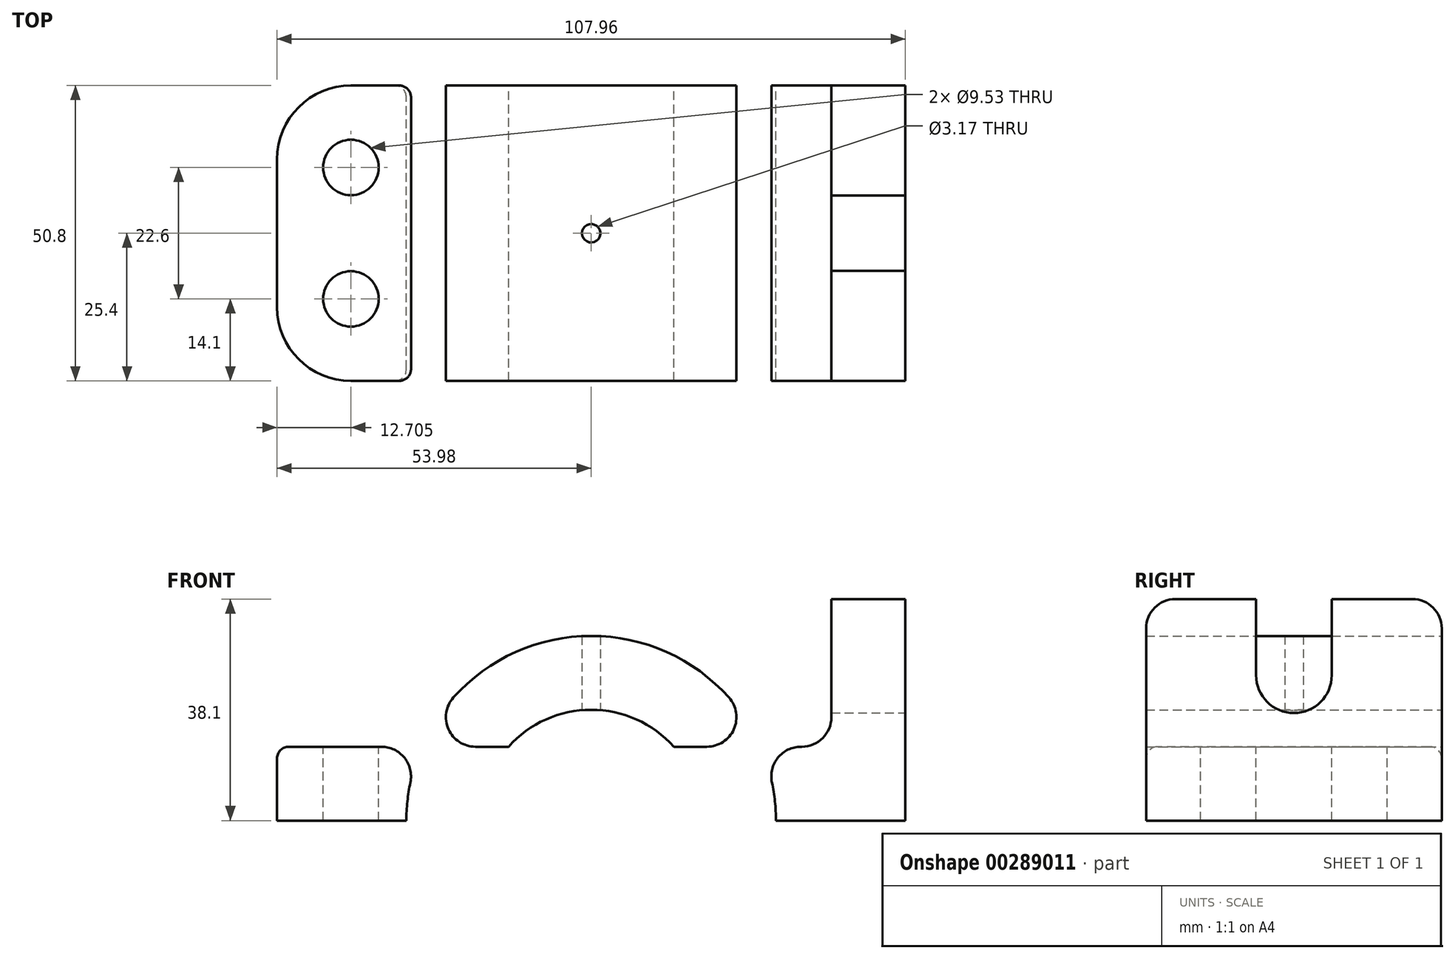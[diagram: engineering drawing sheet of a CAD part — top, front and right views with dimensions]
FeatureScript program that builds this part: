
annotation { "Feature Type Name" : "Feature", "Feature Type Description" : "" }
export const myFeature = defineFeature(function(context is Context, id is Id, definition is map)
    precondition{}
    {
        {
            var Q0;
            Q0=qCreatedBy(makeId("Front.planeOp"),FACE);
            var sketch = newSketch(context, id + "F0", { "sketchPlane" : qUnion([Q0])});
            skLineSegment(sketch, "E0", {"start": v(-53.97, 0) * mm, "end": v(53.97, 0) * mm});
            skLineSegment(sketch, "E1", {"start": v(53.98, 0) * mm, "end": v(53.98, 38.1) * mm});
            skLineSegment(sketch, "E2", {"start": v(53.97, 38.1) * mm, "end": v(41.28, 38.1) * mm});
            skLineSegment(sketch, "E3", {"start": v(41.28, 38.1) * mm, "end": v(41.28, 12.7) * mm});
            skLineSegment(sketch, "E4", {"start": v(41.28, 12.7) * mm, "end": v(-53.98, 12.7) * mm});
            skLineSegment(sketch, "E5", {"start": v(-53.98, 12.7) * mm, "end": v(-53.98, 0) * mm});
            skCircle(sketch, "E6", {"center": v(0, 0) * mm, "radius": 31.75 * mm});
            skCircle(sketch, "E7", {"center": v(0, 0) * mm, "radius": 19.05 * mm});
            skSolve(sketch);
        }
        {
            var Q0;
            {var subQ5=sQuery(id+"F0.wireOp",EDGE,"E5");Q0=makeQuery(id+"F0.imprint","IMPRINT",FACE,{"disambiguationData":[TD([[makeQuery(id+"F0.imprint","IMPRINT",EDGE,{"derivedFrom":subQ5}),1.0]])]});}
            var Q1;
            {var subQ6=sQuery(id+"F0.wireOp",EDGE,"E1");Q1=makeQuery(id+"F0.imprint","IMPRINT",FACE,{"disambiguationData":[TD([[makeQuery(id+"F0.imprint","IMPRINT",EDGE,{"derivedFrom":subQ6}),1.0]])]});}
            var Q2;
            {var subQ1=sQuery(id+"F0.wireOp",EDGE,"E4");var subQ4=sQuery(id+"F0.wireOp",EDGE,"E6");var subQ6=makeQuery(id+"F0.imprint","INTERSECT",VERTEX,{"disambiguationData":[OD(0.0)],"derivedFrom":[subQ1,subQ4]});Q2=makeQuery(id+"F0.imprint","IMPRINT",FACE,{"disambiguationData":[TD([[makeQuery(id+"F0.imprint","IMPRINT",EDGE,{"disambiguationData":[TD([[subQ6,-1.0]])],"derivedFrom":subQ1}),-1.0]])]});}
            var Q3;
            {var subQ3=sQuery(id+"F0.wireOp",EDGE,"E0");var subQ5=sQuery(id+"F0.wireOp",EDGE,"E6");var subQ7=makeQuery(id+"F0.imprint","INTERSECT",VERTEX,{"disambiguationData":[OD(1.0)],"derivedFrom":[subQ3,subQ5]});Q3=makeQuery(id+"F0.imprint","IMPRINT",FACE,{"disambiguationData":[TD([[makeQuery(id+"F0.imprint","IMPRINT",EDGE,{"disambiguationData":[TD([[subQ7,1.0]])],"derivedFrom":subQ3}),1.0]])]});}
            var Q4;
            {var subQ3=sQuery(id+"F0.wireOp",EDGE,"E0");var subQ5=sQuery(id+"F0.wireOp",EDGE,"E6");var subQ7=makeQuery(id+"F0.imprint","INTERSECT",VERTEX,{"disambiguationData":[OD(0.0)],"derivedFrom":[subQ3,subQ5]});Q4=makeQuery(id+"F0.imprint","IMPRINT",FACE,{"disambiguationData":[TD([[makeQuery(id+"F0.imprint","IMPRINT",EDGE,{"disambiguationData":[TD([[subQ7,-1.0]])],"derivedFrom":subQ3}),1.0]])]});}
            extrude(context, id + "F1", {"entities" : qUnion([Q0, Q1, Q2, Q3, Q4]), "endBound" : BoundingType.SYMMETRIC, "depth" : 50.8 * mm});
        }
        {
            var Q0;
            {var subQ0=sQuery(id+"F0.wireOp",EDGE,"E4");Q0=makeQuery(id+"F1.opExtrude","SWEPT_FACE",FACE,{"disambiguationData":[OSD([subQ0]),TDD([makeQuery(id+"F0.imprint","IMPRINT",EDGE,{"disambiguationData":[TD([[makeQuery(id+"F0.imprint","INTERSECT",VERTEX,{"derivedFrom":[subQ0,sQuery(id+"F0.wireOp",EDGE,"E5")]}),1.0]])],"derivedFrom":subQ0})])]});}
            var sketch = newSketch(context, id + "F2", { "sketchPlane" : qUnion([Q0])});
            skCircle(sketch, "E8", {"center": v(-41.27, 11.3) * mm, "radius": 4.76 * mm});
            skCircle(sketch, "E9", {"center": v(-41.27, -11.3) * mm, "radius": 4.76 * mm});
            skSolve(sketch);
        }
        {
            var Q0;
            {Q0=qUnion([makeQuery(id+"F2.imprint","IMPRINT",FACE,{"disambiguationData":[TD([[makeQuery(id+"F2.imprint","IMPRINT",EDGE,{"derivedFrom":sQuery(id+"F2.wireOp",EDGE,"E8")}),1.0]])]}),makeQuery(id+"F2.imprint","IMPRINT",FACE,{"disambiguationData":[TD([[makeQuery(id+"F2.imprint","IMPRINT",EDGE,{"derivedFrom":sQuery(id+"F2.wireOp",EDGE,"E9")}),1.0]])]})]);}
            extrude(context, id + "F3", {"entities" : qUnion([Q0]), "operationType" : NewBodyOperationType.REMOVE, "endBound" : BoundingType.THROUGH_ALL, "oppositeDirection" : true, "depth" : 25 * mm});
        }
        {
            var Q0;
            Q0=makeQuery(id+"F1.opExtrude","SWEPT_FACE",FACE,{"disambiguationData":[OSD([sQuery(id+"F0.wireOp",EDGE,"E1")])]});
            var sketch = newSketch(context, id + "F4", { "sketchPlane" : qUnion([Q0])});
            skLineSegment(sketch, "E10.bottom", {"start": v(-6.5, 38.1) * mm, "end": v(6.5, 38.1) * mm});
            skLineSegment(sketch, "E10.top", {"start": v(-6.5, 25) * mm, "end": v(6.5, 25) * mm});
            skLineSegment(sketch, "E10.left", {"start": v(-6.5, 38.1) * mm, "end": v(-6.5, 25) * mm});
            skLineSegment(sketch, "E10.right", {"start": v(6.5, 38.1) * mm, "end": v(6.5, 25) * mm});
            skPoint(sketch, "E11", {"position": v(0, 38.1) * mm});
            skCircle(sketch, "E12", {"center": v(0, 25) * mm, "radius": 6.5 * mm});
            skSolve(sketch);
        }
        {
            var Q0;
            {var subQ1=sQuery(id+"F4.wireOp",EDGE,"E10.top");var subQ7=makeQuery(id+"F4.imprint","IMPRINT",EDGE,{"derivedFrom":subQ1});Q0=qUnion([makeQuery(id+"F4.imprint","IMPRINT",FACE,{"disambiguationData":[TD([[makeQuery(id+"F4.imprint","IMPRINT",EDGE,{"derivedFrom":sQuery(id+"F4.wireOp",EDGE,"E10.bottom")}),-1.0]])]}),makeQuery(id+"F4.imprint","IMPRINT",FACE,{"disambiguationData":[TD([[subQ7,1.0]])]}),makeQuery(id+"F4.imprint","IMPRINT",FACE,{"disambiguationData":[TD([[subQ7,-1.0]])]})]);}
            extrude(context, id + "F5", {"entities" : qUnion([Q0]), "operationType" : NewBodyOperationType.REMOVE, "endBound" : BoundingType.UP_TO_NEXT, "oppositeDirection" : true, "depth" : 25 * mm});
        }
        {
            var Q0;
            {var subQ0=sQuery(id+"F0.wireOp",EDGE,"E0");var subQ1=makeQuery(id+"F0.imprint","INTERSECT",VERTEX,{"disambiguationData":[OD(1.0)],"derivedFrom":[subQ0,sQuery(id+"F0.wireOp",EDGE,"E6")]});Q0=makeQuery(id+"F1.opExtrude","SWEPT_FACE",FACE,{"disambiguationData":[OSD([subQ0]),TDD([makeQuery(id+"F0.imprint","IMPRINT",EDGE,{"disambiguationData":[TD([[subQ1,1.0]])],"derivedFrom":subQ0}),makeQuery(id+"F0.imprint","IMPRINT",EDGE,{"disambiguationData":[TD([[makeQuery(id+"F0.imprint","INTERSECT",VERTEX,{"derivedFrom":[subQ0,sQuery(id+"F0.wireOp",EDGE,"E1")]}),1.0]])],"derivedFrom":subQ0})])]});}
            var sketch = newSketch(context, id + "F6", { "sketchPlane" : qUnion([Q0])});
            skCircle(sketch, "E13", {"center": v(0, 0) * mm, "radius": 1.59 * mm});
            skSolve(sketch);
        }
        {
            var Q0;
            Q0=makeQuery(id+"F6.imprint","IMPRINT",FACE,{"disambiguationData":[TD([[makeQuery(id+"F6.imprint","IMPRINT",EDGE,{"derivedFrom":sQuery(id+"F6.wireOp",EDGE,"E13")}),1.0]])]});
            extrude(context, id + "F7", {"entities" : qUnion([Q0]), "operationType" : NewBodyOperationType.REMOVE, "endBound" : BoundingType.THROUGH_ALL, "oppositeDirection" : true, "depth" : 47.28 * mm});
        }
        {
            var Q0;
            Q0=makeQuery(id+"F1.opExtrude","CAP_EDGE",EDGE,{"disambiguationData":[OSD([sQuery(id+"F0.wireOp",EDGE,"E2")])],"isStart":false});
            var Q1;
            Q1=makeQuery(id+"F1.opExtrude","CAP_EDGE",EDGE,{"disambiguationData":[OSD([sQuery(id+"F0.wireOp",EDGE,"E2")])],"isStart":true});
            var Q2;
            {var subQ0=sQuery(id+"F0.wireOp",EDGE,"E4");var subQ1=sQuery(id+"F0.wireOp",EDGE,"E6");Q2=makeQuery(id+"F1.opExtrude","SWEPT_EDGE",EDGE,{"disambiguationData":[OSD([subQ0,subQ1]),TDD([makeQuery(id+"F0.imprint","INTERSECT",VERTEX,{"disambiguationData":[OD(0.0)],"derivedFrom":[subQ0,subQ1]})])]});}
            var Q3;
            Q3=makeQuery(id+"F1.opExtrude","SWEPT_EDGE",EDGE,{"disambiguationData":[OSD([sQuery(id+"F0.wireOp",EDGE,"E3"),sQuery(id+"F0.wireOp",EDGE,"E4")])]});
            var Q4;
            {var subQ0=sQuery(id+"F0.wireOp",EDGE,"E4");var subQ1=sQuery(id+"F0.wireOp",EDGE,"E6");Q4=makeQuery(id+"F1.opExtrude","SWEPT_EDGE",EDGE,{"disambiguationData":[OSD([subQ0,subQ1]),TDD([makeQuery(id+"F0.imprint","INTERSECT",VERTEX,{"disambiguationData":[OD(1.0)],"derivedFrom":[subQ0,subQ1]})])]});}
            fillet(context, id + "F8", {"entities" : qUnion([Q0, Q1, Q2, Q3, Q4]), "radius" : 5.08 * mm, "tangentPropagation" : true, "allowEdgeOverflow" : false});
        }
        {
            var Q0;
            Q0=makeQuery(id+"F1.opExtrude","CAP_EDGE",EDGE,{"disambiguationData":[OSD([sQuery(id+"F0.wireOp",EDGE,"E5")])],"isStart":true});
            var Q1;
            Q1=makeQuery(id+"F1.opExtrude","CAP_EDGE",EDGE,{"disambiguationData":[OSD([sQuery(id+"F0.wireOp",EDGE,"E5")])],"isStart":false});
            fillet(context, id + "F9", {"entities" : qUnion([Q0, Q1]), "radius" : 12.7 * mm, "tangentPropagation" : true, "allowEdgeOverflow" : false});
        }
        {
            var Q0;
            {var subQ0=sQuery(id+"F0.wireOp",EDGE,"E4");Q0=makeQuery(id+"F1.opExtrude","CAP_EDGE",EDGE,{"disambiguationData":[OSD([subQ0]),TDD([makeQuery(id+"F0.imprint","IMPRINT",EDGE,{"disambiguationData":[TD([[makeQuery(id+"F0.imprint","INTERSECT",VERTEX,{"derivedFrom":[subQ0,sQuery(id+"F0.wireOp",EDGE,"E5")]}),1.0]])],"derivedFrom":subQ0})])],"isStart":false});}
            fillet(context, id + "F10", {"entities" : qUnion([Q0]), "radius" : 2.03 * mm, "tangentPropagation" : true, "allowEdgeOverflow" : false});
        }
    });
